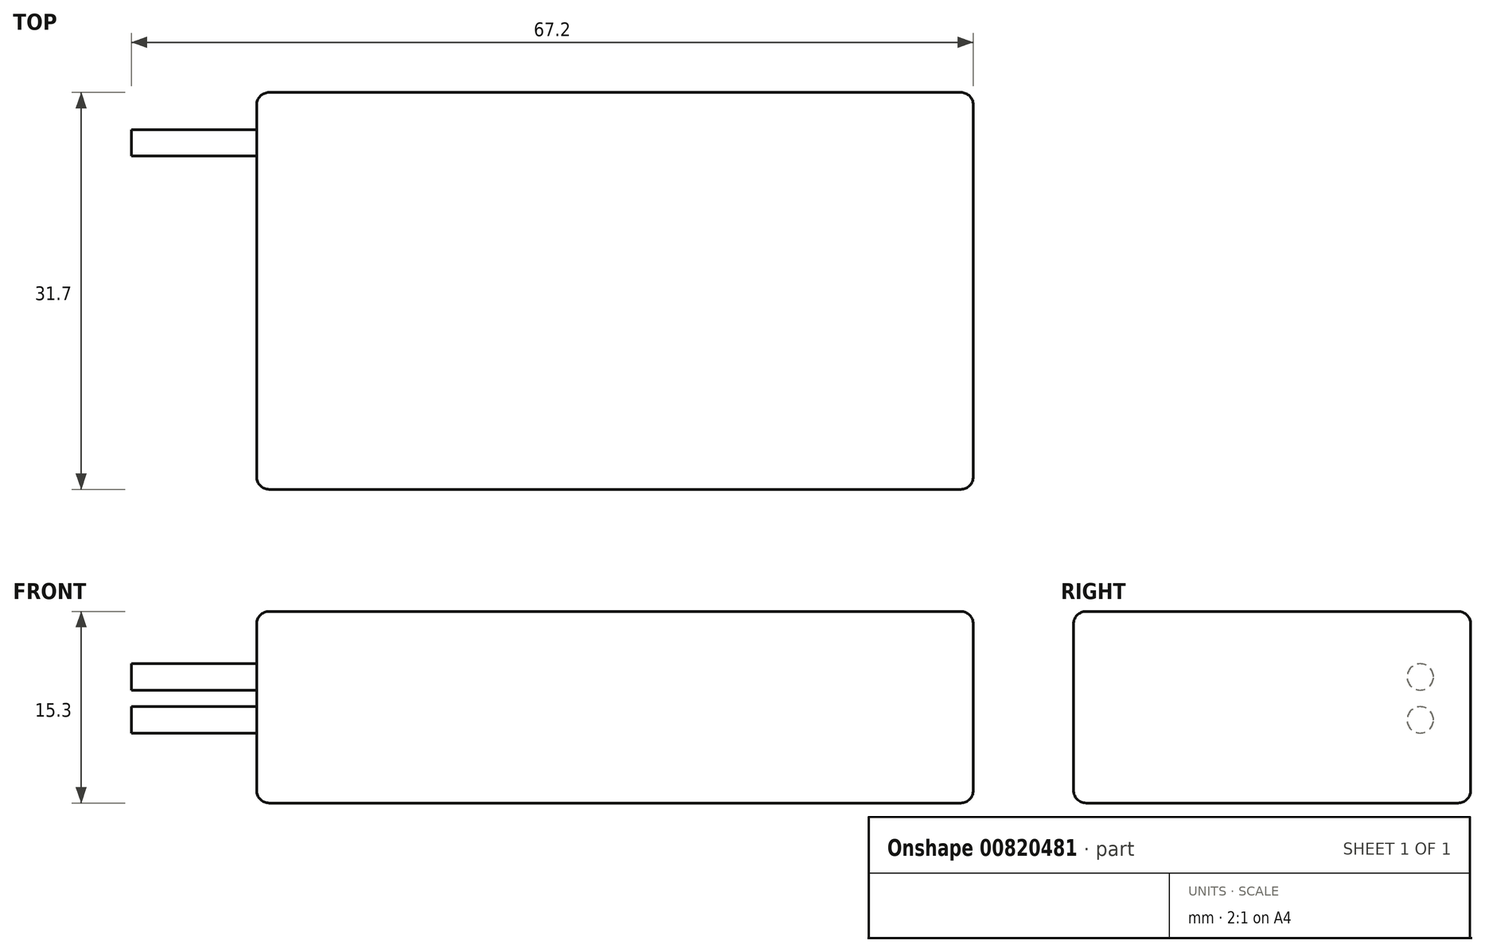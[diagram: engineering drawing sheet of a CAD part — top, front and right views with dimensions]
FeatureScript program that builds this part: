
annotation { "Feature Type Name" : "Feature", "Feature Type Description" : "" }
export const myFeature = defineFeature(function(context is Context, id is Id, definition is map)
    precondition{}
    {
        {
            var Q0;
            Q0=qCreatedBy(makeId("Top.planeOp"),FACE);
            var sketch = newSketch(context, id + "F0", { "sketchPlane" : qUnion([Q0])});
            skLineSegment(sketch, "E0.bottom", {"start": v(28.6, 15.85) * mm, "end": v(-28.6, 15.85) * mm});
            skLineSegment(sketch, "E0.top", {"start": v(28.6, -15.85) * mm, "end": v(-28.6, -15.85) * mm});
            skLineSegment(sketch, "E0.left", {"start": v(28.6, 15.85) * mm, "end": v(28.6, -15.85) * mm});
            skLineSegment(sketch, "E0.right", {"start": v(-28.6, 15.85) * mm, "end": v(-28.6, -15.85) * mm});
            skPoint(sketch, "E0.middle", {"position": v(0, 0) * mm});
            skSolve(sketch);
        }
        {
            var Q0;
            Q0=makeQuery(id+"F0.imprint","IMPRINT",FACE,{"disambiguationData":[TD([[makeQuery(id+"F0.imprint","IMPRINT",EDGE,{"derivedFrom":sQuery(id+"F0.wireOp",EDGE,"E0.bottom")}),1.0]])]});
            extrude(context, id + "F1", {"entities" : qUnion([Q0]), "depth" : 15.3 * mm, "offsetDistance" : 25 * mm});
        }
        {
            var Q0;
            Q0=makeQuery(id+"F1.opExtrude","CAP_EDGE",EDGE,{"disambiguationData":[OSD([sQuery(id+"F0.wireOp",EDGE,"E0.top")])],"isStart":false});
            var Q1;
            Q1=makeQuery(id+"F1.opExtrude","SWEPT_EDGE",EDGE,{"disambiguationData":[OSD([sQuery(id+"F0.wireOp",EDGE,"E0.bottom"),sQuery(id+"F0.wireOp",EDGE,"E0.left")])]});
            var Q2;
            Q2=makeQuery(id+"F1.opExtrude","SWEPT_EDGE",EDGE,{"disambiguationData":[OSD([sQuery(id+"F0.wireOp",EDGE,"E0.top"),sQuery(id+"F0.wireOp",EDGE,"E0.left")])]});
            var Q3;
            Q3=makeQuery(id+"F1.opExtrude","SWEPT_EDGE",EDGE,{"disambiguationData":[OSD([sQuery(id+"F0.wireOp",EDGE,"E0.top"),sQuery(id+"F0.wireOp",EDGE,"E0.right")])]});
            var Q4;
            Q4=makeQuery(id+"F1.opExtrude","CAP_EDGE",EDGE,{"disambiguationData":[OSD([sQuery(id+"F0.wireOp",EDGE,"E0.bottom")])],"isStart":false});
            var Q5;
            Q5=makeQuery(id+"F1.opExtrude","CAP_EDGE",EDGE,{"disambiguationData":[OSD([sQuery(id+"F0.wireOp",EDGE,"E0.top")])],"isStart":true});
            var Q6;
            Q6=makeQuery(id+"F1.opExtrude","SWEPT_EDGE",EDGE,{"disambiguationData":[OSD([sQuery(id+"F0.wireOp",EDGE,"E0.bottom"),sQuery(id+"F0.wireOp",EDGE,"E0.right")])]});
            var Q7;
            Q7=makeQuery(id+"F1.opExtrude","CAP_EDGE",EDGE,{"disambiguationData":[OSD([sQuery(id+"F0.wireOp",EDGE,"E0.bottom")])],"isStart":true});
            var Q8;
            Q8=makeQuery(id+"F1.opExtrude","CAP_EDGE",EDGE,{"disambiguationData":[OSD([sQuery(id+"F0.wireOp",EDGE,"E0.left")])],"isStart":true});
            var Q9;
            Q9=makeQuery(id+"F1.opExtrude","CAP_EDGE",EDGE,{"disambiguationData":[OSD([sQuery(id+"F0.wireOp",EDGE,"E0.left")])],"isStart":false});
            var Q10;
            Q10=makeQuery(id+"F1.opExtrude","CAP_EDGE",EDGE,{"disambiguationData":[OSD([sQuery(id+"F0.wireOp",EDGE,"E0.right")])],"isStart":true});
            var Q11;
            Q11=makeQuery(id+"F1.opExtrude","CAP_EDGE",EDGE,{"disambiguationData":[OSD([sQuery(id+"F0.wireOp",EDGE,"E0.right")])],"isStart":false});
            fillet(context, id + "F2", {"entities" : qUnion([Q0, Q1, Q2, Q3, Q4, Q5, Q6, Q7, Q8, Q9, Q10, Q11]), "radius" : 1 * mm, "tangentPropagation" : true, "allowEdgeOverflow" : false});
        }
        {
            var Q0;
            Q0=makeQuery(id+"F1.opExtrude","SWEPT_FACE",FACE,{"disambiguationData":[OSD([sQuery(id+"F0.wireOp",EDGE,"E0.right")])]});
            var sketch = newSketch(context, id + "F3", { "sketchPlane" : qUnion([Q0])});
            skCircle(sketch, "E1", {"center": v(-11.83, 10.07) * mm, "radius": 1.05 * mm});
            skCircle(sketch, "E2", {"center": v(-11.83, 6.64) * mm, "radius": 1.05 * mm});
            skSolve(sketch);
        }
        {
            var Q0;
            Q0=makeQuery(id+"F3.imprint","IMPRINT",FACE,{"disambiguationData":[TD([[makeQuery(id+"F3.imprint","IMPRINT",EDGE,{"derivedFrom":sQuery(id+"F3.wireOp",EDGE,"E1")}),1.0]])]});
            var Q1;
            Q1=makeQuery(id+"F3.imprint","IMPRINT",FACE,{"disambiguationData":[TD([[makeQuery(id+"F3.imprint","IMPRINT",EDGE,{"derivedFrom":sQuery(id+"F3.wireOp",EDGE,"E2")}),1.0]])]});
            extrude(context, id + "F4", {"entities" : qUnion([Q0, Q1]), "depth" : 10 * mm, "offsetDistance" : 25 * mm});
        }
    });
